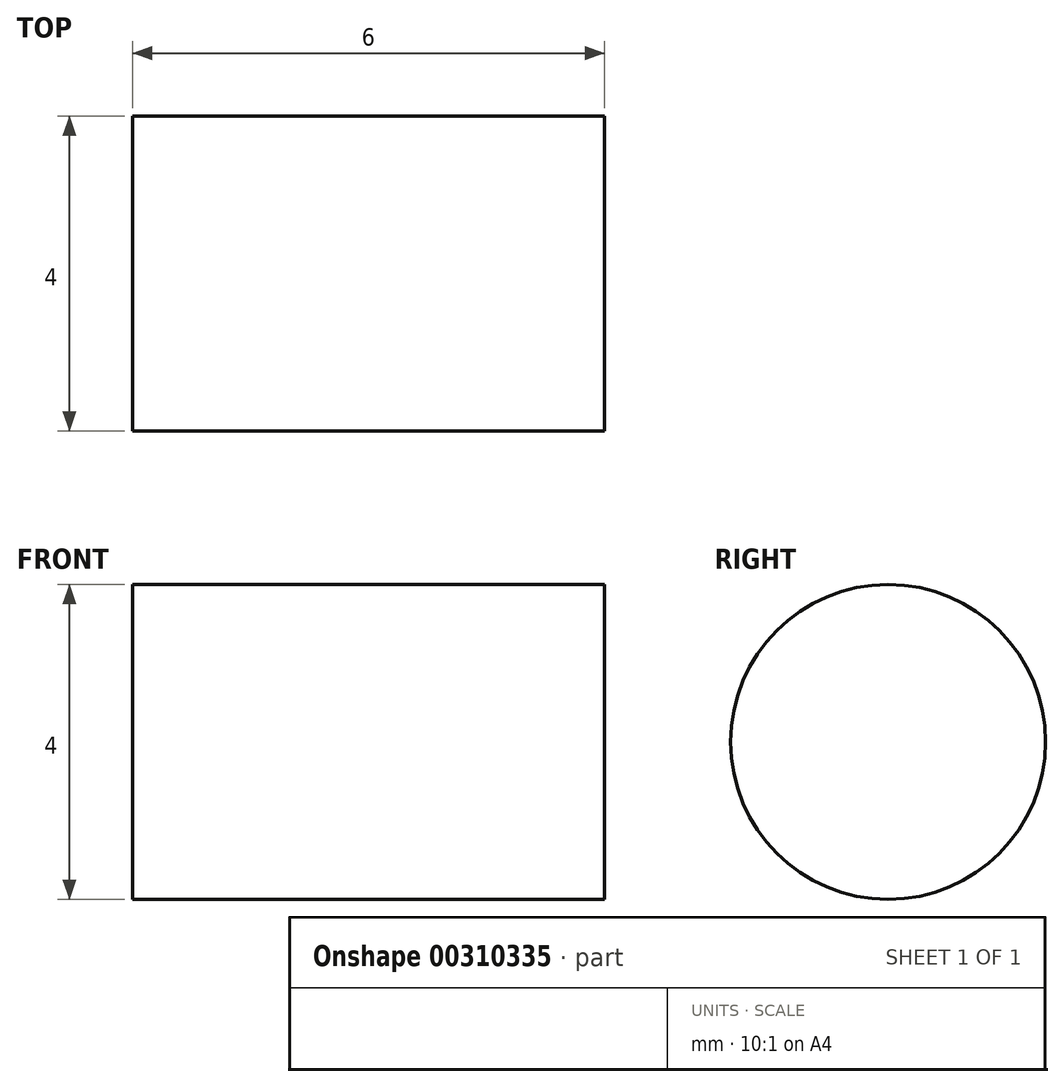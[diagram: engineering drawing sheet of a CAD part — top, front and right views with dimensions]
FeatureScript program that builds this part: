
annotation { "Feature Type Name" : "Feature", "Feature Type Description" : "" }
export const myFeature = defineFeature(function(context is Context, id is Id, definition is map)
    precondition{}
    {
        {
            var Q0;
            Q0=qCreatedBy(makeId("Right.planeOp"),FACE);
            var sketch = newSketch(context, id + "F0", { "sketchPlane" : qUnion([Q0])});
            skCircle(sketch, "E0", {"center": v(0, 0) * mm, "radius": 2 * mm});
            skSolve(sketch);
        }
        {
            var Q0;
            Q0 = qSketchRegion(id + "F0", true);
            extrude(context, id + "F1", {"entities" : qUnion([Q0]), "depth" : 6 * mm, "offsetDistance" : 25 * mm});
        }
    });
